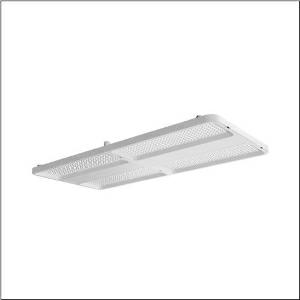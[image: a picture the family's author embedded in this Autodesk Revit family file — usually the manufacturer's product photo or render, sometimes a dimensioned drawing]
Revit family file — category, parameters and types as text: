
# Revit family: highbay_11_maxi_51hn12db4lda
name_source: partatom
category: Lighting Fixtures
units: mm (PartAtom-declared; Revit-internal decimal feet)

## family parameters
Cut with Voids When Loaded = No
Host = Face
Light Source = No
Part Type = Normal
Room Calculation Point = No
Round Connector Dimension = Use Diameter
Shared = No

## types (1)
- --- (1 x LED, 3960 lm, 19.5 W, 4000K)
    Apparent Load = 20 VA
    CIE Flux Codes = 87 98 100 100 100
    Color Rendering = 80
    Color Temperature = 4000K
    Default Elevation = 1800 mm
    Description = high bay luminaire Highbay 11 maxi; direct symmetric wide distribution, light control with lens of PMMA; UGR ≤ 19 (X = 4H | Y = 8H | S = 0.25H | reflection values 70/50/20); luminous flux: 26.000lm; light colour: 840, colour temperature: 4000K, MacAdam ≤ 2 SDCM (initial), colour rendering: CRI > 80; luminous efficacy: 207,3lm/W; rated service life: 100.000h (L95/B50) at AT= 25°C; control: DALI 2; housing frame of high-performance plastic PA6, matt traffic white (RAL 9016); cover of PMMA; dimension (LxWxH): 946 x 442 x 72mm; luminaire connection: terminal, 5-pole, max. 2.5mm² (cable entry for one cable, Ø 8.5..16mm); mains connection: 230..240V, AC/DC 0/50..60Hz; connected load: 125,4W; protection rating (complete): IP66; insulation class (complete): insulation class I (protective earthing); protection symbol: D; impact resistance: IK08; halogen-free wiring; for central battery installations according to DIN EN 60598-2-22; corresponds to IFS (International Featured Standards) requirements for safety and quality in the food industry; LABS conformity tested according to VDMA 24364:2018-05; certification: CE, ENEC, VDE, UKCA; permissible operating ambient temperature: -40..+65°C (reducing of maximum allowable ambient temperature of 5°C with ceiling mounting); packaging unit: 1 piece; (delivery without accessories; please order mounting accessories separately)
    Height = 72 mm  [stored 0.23622 ft]
    Lamp = 1 x LED
    Lamp Light Flux = 3960 lm
    Lamp Power = 19.5 W
    Lamp count = 1
    Length = 946 mm
    Luminous efficacy = 203 lm/W
    Manufacturer = Siteco
    ModVariant = No
    Model = 51HN12DB4LDA
    Mounting Place = Ceiling
    Mounting Type = Pendant
    Number of Poles = 1
    OnlyDefault = Yes
    Power Factor = 1
    Product Name = Highbay 11 maxi
    Product group = high bay luminaire
    ProductGroupID = 901
    Protection Class = Protection class I
    Protection Degree = IP 66
    RLX_Detail_Level = 1
    RLX_Emergency_Light_Flux = 0 lm
    RLX_Emergency_Type = 0
    RLX_Emergency_Type_DB = No
    RlxData = <blob elided: 22133 chars, md5=bf0fcfd3>
    Socket = socket
    Standby Power = 0 W
    System Light Flux = 3960 lm
    System Power = 20 W
    Type Comments = : DC mode (central or group accumulator) initial emergency light level
    Type Image = l_1363244.jpg
    URL = http://relux.com
    VarID = @adj_005165
    Voltage = 0 V
    Weight = 0.00 kg
    Width = 442 mm

note: [stored X ft] marks values corroborated as IEEE doubles in the binary element streams (Revit-internal decimal feet)

## geometry (parser evidence)
native form markers: Blend x4, Sweep x11
no freeform markers — native parametric forms only
